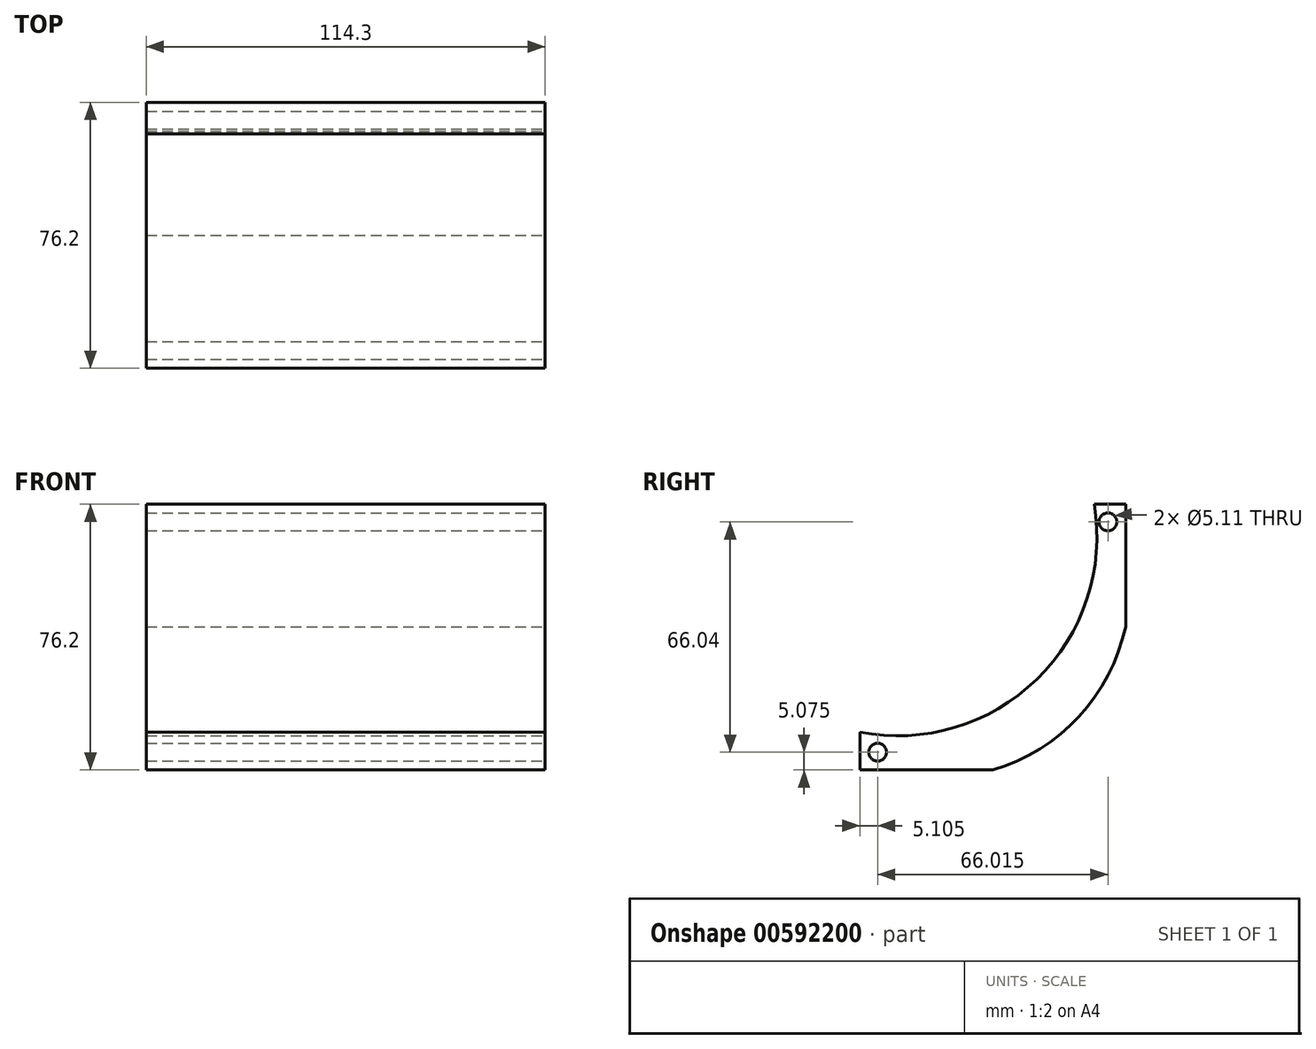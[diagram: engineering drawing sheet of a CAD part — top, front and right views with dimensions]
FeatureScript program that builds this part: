
annotation { "Feature Type Name" : "Feature", "Feature Type Description" : "" }
export const myFeature = defineFeature(function(context is Context, id is Id, definition is map)
    precondition{}
    {
        {
            var Q0;
            Q0=qCreatedBy(makeId("Front.planeOp"),FACE);
            var sketch = newSketch(context, id + "F0", { "sketchPlane" : qUnion([Q0])});
            skLineSegment(sketch, "E0.bottom", {"start": v(-56.33, 35.14) * mm, "end": v(57.97, 35.14) * mm});
            skLineSegment(sketch, "E0.top", {"start": v(-56.33, -41.06) * mm, "end": v(57.97, -41.06) * mm});
            skLineSegment(sketch, "E0.left", {"start": v(-56.33, 35.14) * mm, "end": v(-56.33, -41.06) * mm});
            skLineSegment(sketch, "E0.right", {"start": v(57.97, 35.14) * mm, "end": v(57.97, -41.06) * mm});
            skSolve(sketch);
        }
        {
            var Q0;
            Q0 = qSketchRegion(id + "F0", true);
            extrude(context, id + "F1", {"entities" : qUnion([Q0]), "depth" : 76.2 * mm, "offsetDistance" : 25.4 * mm});
        }
        {
            var Q0;
            Q0=makeQuery(id+"F1.opExtrude","SWEPT_FACE",FACE,{"disambiguationData":[OSD([sQuery(id+"F0.wireOp",EDGE,"E0.right")])]});
            var sketch = newSketch(context, id + "F2", { "sketchPlane" : qUnion([Q0])});
            skArc(sketch, "E1", {"start": v(-38.1, -41.06) * mm, "mid": v(-13.4, -25.78) * mm, "end": v(0, 0) * mm});
            skArc(sketch, "E2", {"start": v(-76.2, -30.22) * mm, "mid": v(-25.5, -15.12) * mm, "end": v(-9, 35.14) * mm});
            skCircle(sketch, "E3", {"center": v(-71.1, -35.98) * mm, "radius": 2.55 * mm});
            skCircle(sketch, "E4", {"center": v(-5.08, 30.06) * mm, "radius": 2.55 * mm});
            skSolve(sketch);
        }
        {
            var Q0;
            Q0 = qSketchRegion(id + "F2", true);
            var Q1;
            Q1=makeQuery(id+"F2.imprint","IMPRINT",FACE,{"disambiguationData":[TD([[makeQuery(id+"F2.imprint","IMPRINT",EDGE,{"derivedFrom":sQuery(id+"F2.wireOp",EDGE,"d3CuC5d1-cVy8-SyXB-oZNI-xZKM6MNmm5ly")}),1.0]])]});
            var Q2;
            {var subQ0=sQuery(id+"F2.wireOp",EDGE,"E1");Q2=makeQuery(id+"F2.imprint","IMPRINT",FACE,{"disambiguationData":[TD([[makeQuery(id+"F2.imprint","IMPRINT",EDGE,{"derivedFrom":subQ0}),-1.0]])]});}
            var Q3;
            {var subQ0=sQuery(id+"F2.wireOp",EDGE,"E2");Q3=makeQuery(id+"F2.imprint","IMPRINT",FACE,{"disambiguationData":[TD([[makeQuery(id+"F2.imprint","IMPRINT",EDGE,{"derivedFrom":subQ0}),1.0]])]});}
            extrude(context, id + "F3", {"entities" : qUnion([Q0, Q1, Q2, Q3]), "operationType" : NewBodyOperationType.REMOVE, "oppositeDirection" : true, "depth" : 114.3 * mm, "offsetDistance" : 25.4 * mm});
        }
    });
